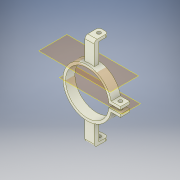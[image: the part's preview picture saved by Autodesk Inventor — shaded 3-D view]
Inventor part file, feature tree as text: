
AUTODESK INVENTOR PART (.ipt)
format: ipt  version: 2019 (Build 230136000, 136)  size: 185,856 bytes
history: native  units: mm
features: extrude x5, sketch x5, plane x3, fillet x1, mirror x1, projected_geometry x1
ambient origin geometry x8: Origin, YZ Plane, XZ Plane, XY Plane, X Axis, Y Axis, Z Axis, Center Point
bodies: Solid1 (feature_tree)
feature tree (16):
  extrude  "Extrusion1"  Depth=52.0mm
  extrude  "Extrusion2"  Depth=10.0mm TaperAngle=0.0deg
  plane  "Work Plane3"
  extrude  "Extrusion3"  Depth=10.0mm TaperAngle=0.0deg
  plane  "Work Plane4"
  extrude  "Extrusion4"  Depth=4.0mm TaperAngle=0.0deg
  plane  "Work Plane2"
  extrude  "Extrusion5"  Depth=10.0mm
  fillet  "Fillet2"  Radius=4.0mm
  mirror  "Mirror3"
  sketch  "Sketch1"  dims[d0=46.5mm d1=52.0mm]
  sketch  "Sketch2"  dims[d10=10.0mm d11=0.0mm d13=11.0mm d14=0.0mm]
  sketch  "Sketch3"  dims[d19=22.5mm d20=0.0mm d23=10.0mm d24=0.0mm]
  sketch  "Sketch4"  dims[d29=4.0mm d30=4.0mm d31=0.0mm]
  sketch  "Sketch5"  dims[d33=3.0mm d34=10.0mm d35=4.0mm d36=15.0mm d37=3.0mm d38=3.0mm]
  projected_geometry  "Projected Loop2"
